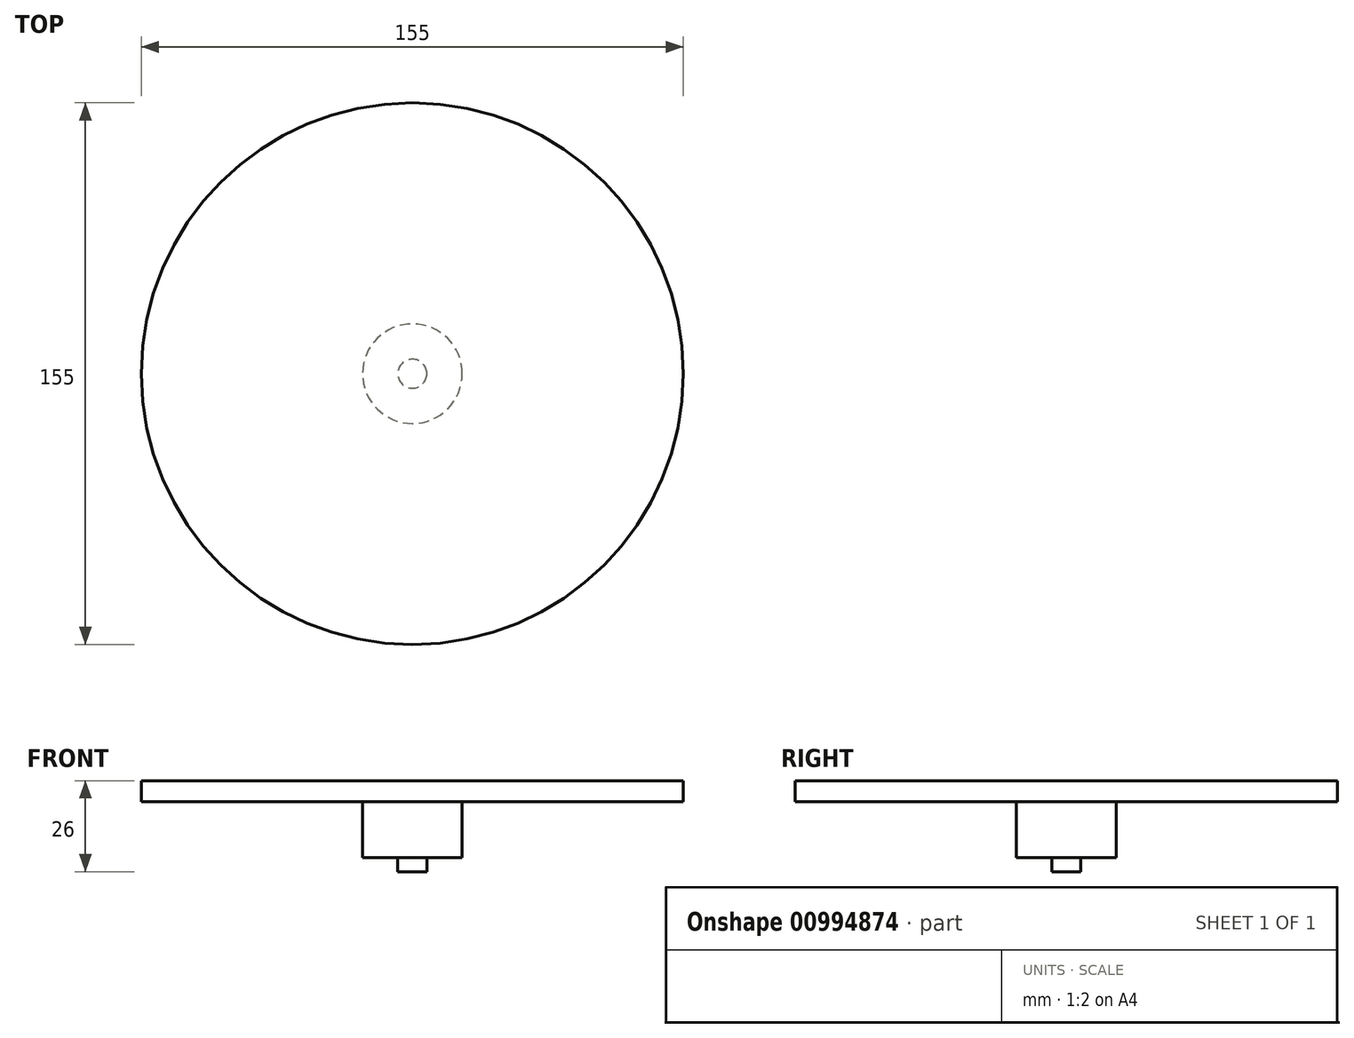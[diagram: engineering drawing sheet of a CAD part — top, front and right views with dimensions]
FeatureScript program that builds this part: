
annotation { "Feature Type Name" : "Feature", "Feature Type Description" : "" }
export const myFeature = defineFeature(function(context is Context, id is Id, definition is map)
    precondition{}
    {
        {
            var Q0;
            Q0=qCreatedBy(makeId("Top.planeOp"),FACE);
            var sketch = newSketch(context, id + "F0", { "sketchPlane" : qUnion([Q0])});
            skCircle(sketch, "E0", {"center": v(0, 0) * mm, "radius": 14.25 * mm});
            skCircle(sketch, "E1", {"center": v(0, 0) * mm, "radius": 2.5 * mm});
            skSolve(sketch);
        }
        {
            var Q0;
            Q0=makeQuery(id+"F0.imprint","IMPRINT",FACE,{"disambiguationData":[TD([[makeQuery(id+"F0.imprint","IMPRINT",EDGE,{"derivedFrom":sQuery(id+"F0.wireOp",EDGE,"E0")}),1.0]])]});
            extrude(context, id + "F1", {"entities" : qUnion([Q0]), "depth" : 16 * mm, "offsetDistance" : 25 * mm});
        }
        {
            var Q0;
            Q0=makeQuery(id+"F0.imprint","IMPRINT",FACE,{"disambiguationData":[TD([[makeQuery(id+"F0.imprint","IMPRINT",EDGE,{"derivedFrom":sQuery(id+"F0.wireOp",EDGE,"E1")}),1.0]])]});
            extrude(context, id + "F2", {"entities" : qUnion([Q0]), "operationType" : NewBodyOperationType.ADD, "depth" : 19 * mm, "offsetDistance" : 25 * mm});
        }
        {
            var Q0;
            Q0=makeQuery(id+"F1.opExtrude","CAP_FACE",FACE,{"disambiguationData":[OSD([sQuery(id+"F0.wireOp",EDGE,"E0"),sQuery(id+"F0.wireOp",EDGE,"E1")])],"isStart":false});
            var sketch = newSketch(context, id + "F3", { "sketchPlane" : qUnion([Q0])});
            skCircle(sketch, "E2", {"center": v(0, 0) * mm, "radius": 77.5 * mm});
            skSolve(sketch);
        }
        {
            var Q0;
            Q0 = qSketchRegion(id + "F3", true);
            extrude(context, id + "F4", {"entities" : qUnion([Q0]), "operationType" : NewBodyOperationType.ADD, "depth" : 6 * mm, "offsetDistance" : 25 * mm});
        }
        {
            var Q0;
            {var subQ0=sQuery(id+"F0.wireOp",EDGE,"E1");Q0=makeQuery(id+"F2.boolean.opBoolean","MERGE",FACE,{"derivedFrom":[makeQuery(id+"F1.opExtrude","CAP_FACE",FACE,{"disambiguationData":[OSD([sQuery(id+"F0.wireOp",EDGE,"E0"),subQ0])],"isStart":true}),makeQuery(id+"F2.opExtrude","CAP_FACE",FACE,{"disambiguationData":[OSD([subQ0])],"isStart":true})]});}
            var sketch = newSketch(context, id + "F5", { "sketchPlane" : qUnion([Q0])});
            skCircle(sketch, "E3", {"center": v(0, 0) * mm, "radius": 4.15 * mm});
            skSolve(sketch);
        }
        {
            var Q0;
            Q0 = qSketchRegion(id + "F5", true);
            extrude(context, id + "F6", {"entities" : qUnion([Q0]), "operationType" : NewBodyOperationType.ADD, "depth" : 4 * mm, "offsetDistance" : 25 * mm});
        }
    });
